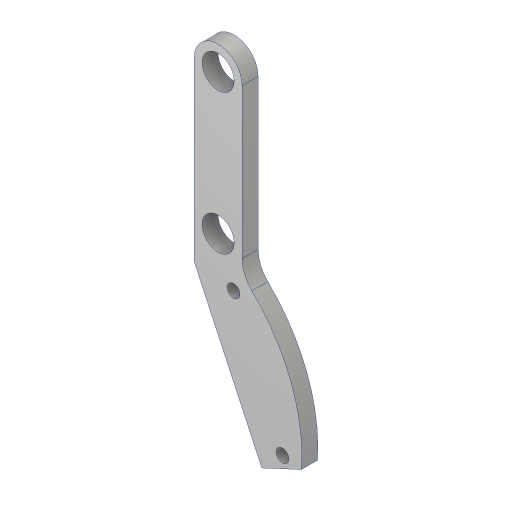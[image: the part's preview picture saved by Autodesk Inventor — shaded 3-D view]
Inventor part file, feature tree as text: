
AUTODESK INVENTOR PART (.ipt)
format: ipt  version: 2023.2 (Build 272271000, 271)  size: 167,424 bytes
history: native  units: mm
features: extrude x4, sketch x4, fillet x2, other x1
ambient origin geometry x8: Origin, YZ Plane, XZ Plane, XY Plane, X Axis, Y Axis, Z Axis, Center Point
bodies: Body1 (feature_tree)
feature tree (11):
  other  "솔리드1"
  extrude  "돌출1"  Depth=20.0mm
  fillet  "모깎기1"  Radius=11.34464mm
  extrude  "돌출2"  Depth=7.0mm
  extrude  "돌출4"  TaperAngle=90.0deg  [1 undecoded]
  extrude  "돌출6"  Depth=20.0mm
  fillet  "모깎기3"  Radius=11.34464mm
  sketch  "스케치1"
  sketch  "스케치2"
  sketch  "스케치4"
  sketch  "스케치6"
note: 1 required parameter value undecoded (feature->parameter linkage not recoverable at this tier; creation-order binding heuristic only, values carry confidence <= 0.55)
